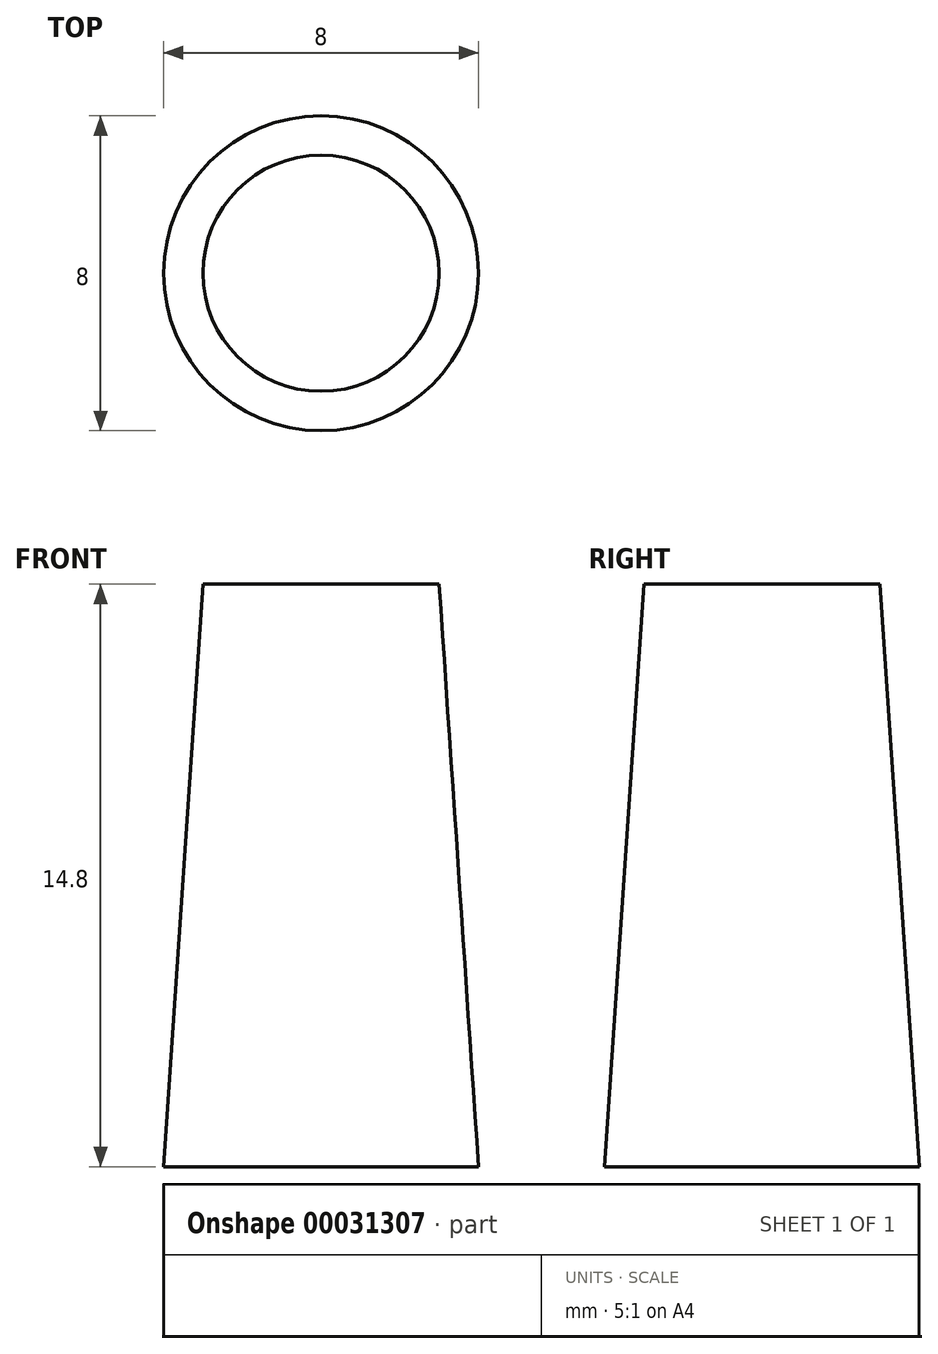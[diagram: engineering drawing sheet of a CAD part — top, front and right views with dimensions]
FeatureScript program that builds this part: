
annotation { "Feature Type Name" : "Feature", "Feature Type Description" : "" }
export const myFeature = defineFeature(function(context is Context, id is Id, definition is map)
    precondition{}
    {
        {
            var Q0;
            Q0=qCreatedBy(makeId("Top.planeOp"),FACE);
            var sketch = newSketch(context, id + "F0", { "sketchPlane" : qUnion([Q0])});
            skCircle(sketch, "E0", {"center": v(0, 0) * mm, "radius": 4 * mm});
            skSolve(sketch);
        }
        {
            var Q0;
            Q0=qCreatedBy(makeId("Top.planeOp"),FACE);
            cPlane(context, id + "F1", {"entities" : qUnion([Q0]), "cplaneType" : CPlaneType.OFFSET, "offset" : 14.8 * mm, "width" : 150 * mm, "height" : 150 * mm});
        }
        {
            var Q0;
            Q0=qCreatedBy(id+"F1.planeOp",FACE);
            var sketch = newSketch(context, id + "F2", { "sketchPlane" : qUnion([Q0])});
            skCircle(sketch, "E1", {"center": v(0, 0) * mm, "radius": 3 * mm});
            skSolve(sketch);
        }
        {
            var Q0;
            Q0=makeQuery(id+"F0.imprint","IMPRINT",FACE,{"disambiguationData":[TD([[makeQuery(id+"F0.imprint","IMPRINT",EDGE,{"derivedFrom":sQuery(id+"F0.wireOp",EDGE,"E0")}),1.0]])]});
            var Q1;
            Q1=makeQuery(id+"F2.imprint","IMPRINT",FACE,{"disambiguationData":[TD([[makeQuery(id+"F2.imprint","IMPRINT",EDGE,{"derivedFrom":sQuery(id+"F2.wireOp",EDGE,"E1")}),1.0]])]});
            loft(context, id + "F3", {"sheetProfilesArray" : [{ "sheetProfileEntities" : qUnion([Q0]) }, { "sheetProfileEntities" : qUnion([Q1]) }]});
        }
    });
